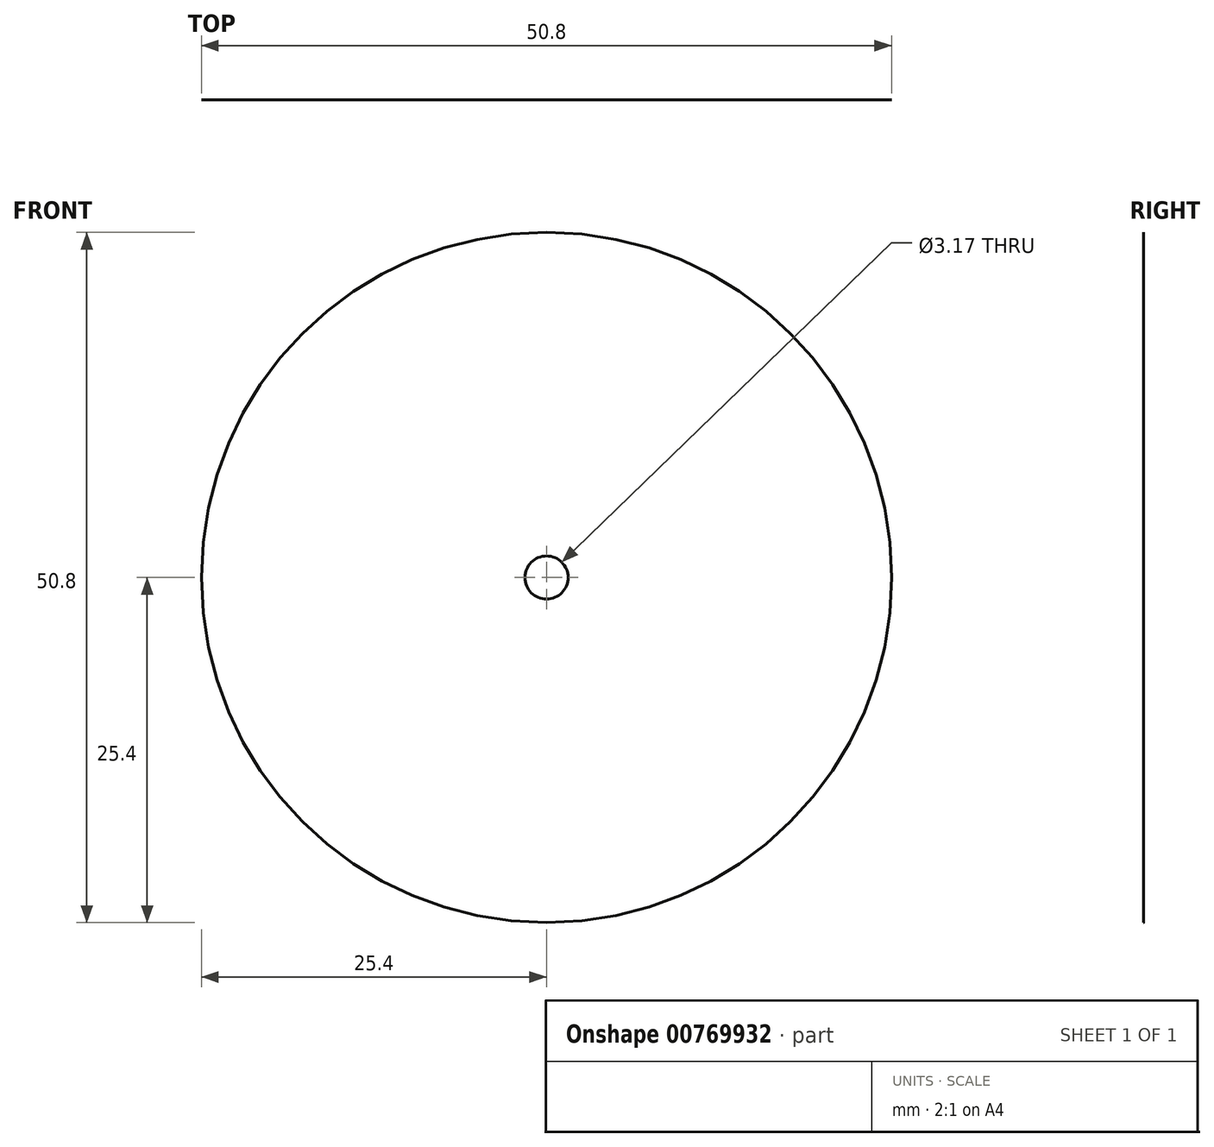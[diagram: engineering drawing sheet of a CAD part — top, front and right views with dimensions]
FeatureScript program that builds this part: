
annotation { "Feature Type Name" : "Feature", "Feature Type Description" : "" }
export const myFeature = defineFeature(function(context is Context, id is Id, definition is map)
    precondition{}
    {
        {
            var Q0;
            Q0=qCreatedBy(makeId("Front.planeOp"),FACE);
            var sketch = newSketch(context, id + "F0", { "sketchPlane" : qUnion([Q0])});
            skCircle(sketch, "E0", {"center": v(0, 0) * mm, "radius": 25.4 * mm});
            skCircle(sketch, "E1", {"center": v(0, 0) * mm, "radius": 22.86 * mm});
            skCircle(sketch, "E2", {"center": v(0, 0) * mm, "radius": 1.59 * mm});
            skCircle(sketch, "E3", {"center": v(0, 0) * mm, "radius": 12.7 * mm});
            skSolve(sketch);
        }
        {
            var Q0;
            Q0 = qSketchRegion(id + "F0", true);
            var Q1;
            {var subQ0=sQuery(id+"F0.wireOp",EDGE,"IZelKgq0-DGtJ-oz25-qGJt-riDNVPKrtG6N");Q1=makeQuery(id+"F0.imprint","IMPRINT",FACE,{"disambiguationData":[TD([[makeQuery(id+"F0.imprint","IMPRINT",EDGE,{"derivedFrom":subQ0}),-1.0]])]});}
            var Q2;
            Q2=makeQuery(id+"F0.imprint","IMPRINT",FACE,{"disambiguationData":[TD([[makeQuery(id+"F0.imprint","IMPRINT",EDGE,{"derivedFrom":sQuery(id+"F0.wireOp",EDGE,"E1")}),1.0]])]});
            var Q3;
            Q3=makeQuery(id+"F0.imprint","IMPRINT",FACE,{"disambiguationData":[TD([[makeQuery(id+"F0.imprint","IMPRINT",EDGE,{"derivedFrom":sQuery(id+"F0.wireOp",EDGE,"E2")}),-1.0]])]});
            extrude(context, id + "F1", {"entities" : qUnion([Q0, Q1, Q2, Q3]), "depth" : 1 / 203.2 * mm, "offsetDistance" : 25.4 * mm});
        }
    });
